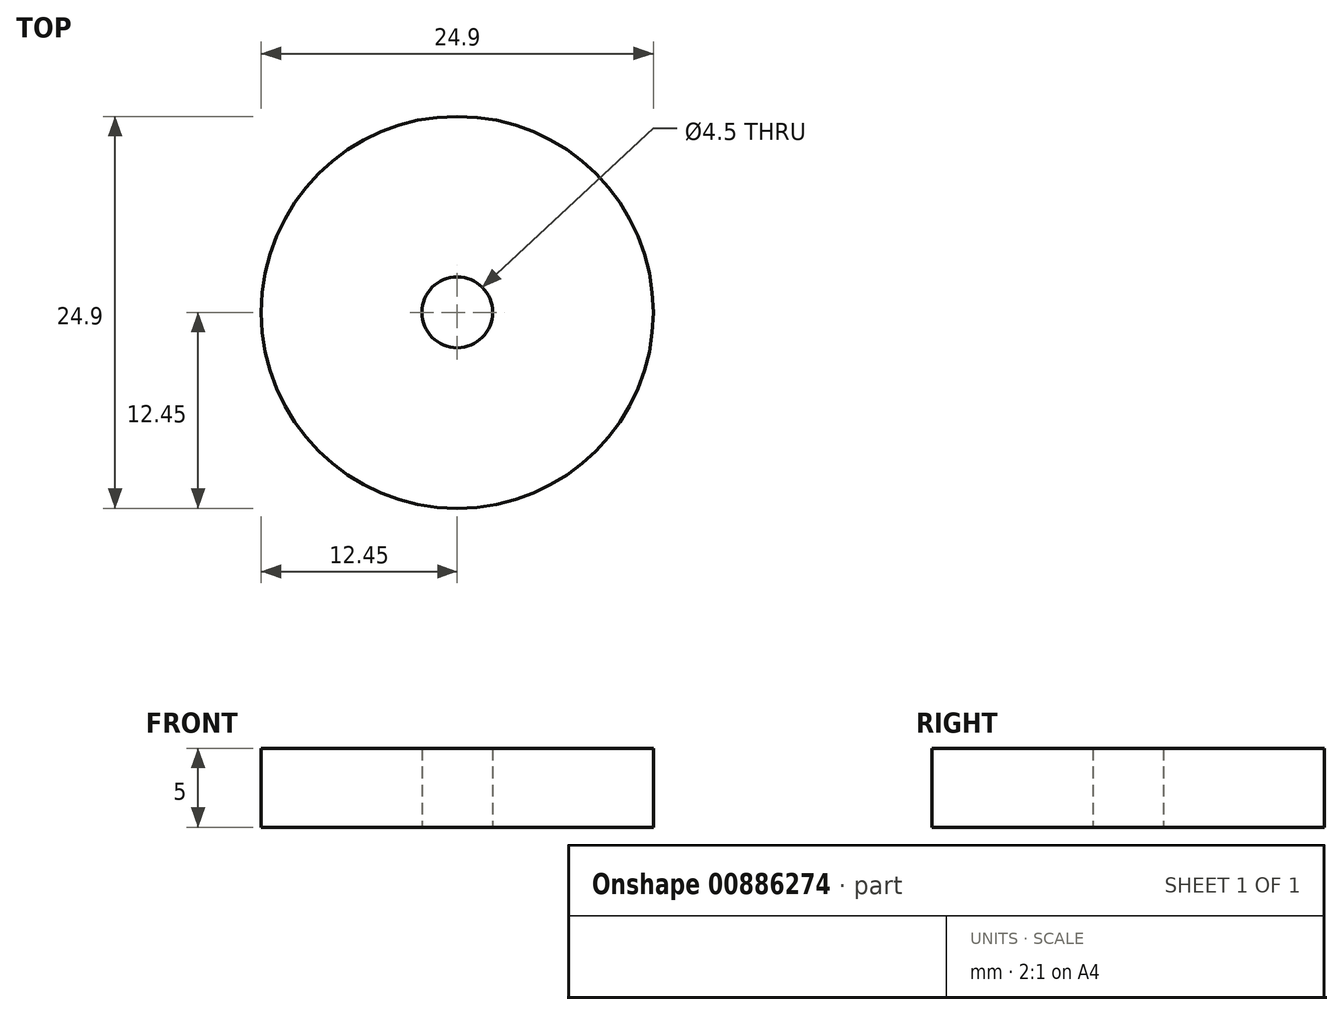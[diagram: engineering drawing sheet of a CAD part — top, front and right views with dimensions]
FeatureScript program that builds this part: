
annotation { "Feature Type Name" : "Feature", "Feature Type Description" : "" }
export const myFeature = defineFeature(function(context is Context, id is Id, definition is map)
    precondition{}
    {
        {
            var Q0;
            Q0=qCreatedBy(makeId("Top.planeOp"),FACE);
            var sketch = newSketch(context, id + "F0", { "sketchPlane" : qUnion([Q0])});
            skCircle(sketch, "E0", {"center": v(0, 0) * mm, "radius": 12.45 * mm});
            skCircle(sketch, "E1", {"center": v(0, 0) * mm, "radius": 2.25 * mm});
            skSolve(sketch);
        }
        {
            var Q0;
            Q0 = qSketchRegion(id + "F0", true);
            extrude(context, id + "F1", {"entities" : qUnion([Q0]), "depth" : 5 * mm, "offsetDistance" : 25 * mm});
        }
    });
